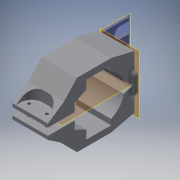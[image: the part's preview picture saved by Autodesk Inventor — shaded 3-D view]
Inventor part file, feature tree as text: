
AUTODESK INVENTOR PART (.ipt)
format: ipt  version: 2016 (Build 200138000, 138)  size: 446,464 bytes
history: native  units: in
note: dims shown in document units (in); Inventor stores cm internally (conversion verified against a paired STEP export)
features: sketch x12, extrude x11, projected_geometry x6, plane x4, reference x4, fillet x3, revolve x1
ambient origin geometry x8: Origin, YZ Plane, XZ Plane, XY Plane, X Axis, Y Axis, Z Axis, Center Point
bodies: Solid1 (feature_tree)
feature tree (41):
  plane  "Work Plane1"
  plane  "Work Plane2"
  extrude  "Extrusion1"  Depth=1.315in
  plane  "Work Plane3"
  extrude  "Extrusion2"  Depth=1.4in
  extrude  "Extrusion3"  Depth=1.8in TaperAngle=0.0deg
  plane  "Work Plane4"
  revolve  "Revolution1"  [1 undecoded]
  fillet  "Fillet1"  Radius=1.925in
  extrude  "Extrusion4"  TaperAngle=90.0deg  [1 undecoded]
  extrude  "Extrusion5"  Depth=0.2in TaperAngle=0.0deg
  extrude  "Extrusion6"  Depth=0.2in TaperAngle=0.0deg
  extrude  "Extrusion7"  Depth=2.575in TaperAngle=0.0deg
  extrude  "Extrusion8"  Depth=0.175in
  extrude  "Extrusion9"  Depth=0.2in TaperAngle=0.0deg
  fillet  "Fillet2"  Radius=0.2in
  fillet  "Fillet3"  Radius=0.625in
  extrude  "Extrusion10"  Depth=0.35in
  extrude  "Extrusion11"  Depth=0.2in
  sketch  "Sketch1"  dims[d2=0.6575in d3=1.315in]
  reference  "Reference1"
  sketch  "Sketch2"  dims[d10=2.92in d11=1.4in]
  sketch  "Sketch3"  dims[d12=0.35in d13=1.8in d14=0.0in]
  reference  "Reference2"
  sketch  "Sketch4"  dims[d15=0.5in d16=0.35in d17=1.925in d18=0.0in]
  reference  "Reference3"
  sketch  "Sketch5"  dims[d19=1.925in d20=0.0in d21=90.0deg]
  projected_geometry  "Projected Loop1"
  reference  "Reference4"
  sketch  "Sketch6"  dims[d22=0.3125in d23=0.2in d24=0.0in]
  projected_geometry  "Projected Loop2"
  sketch  "Sketch7"  dims[d25=1.5in d26=0.2in d27=0.0in]
  projected_geometry  "Projected Loop3"
  sketch  "Sketch8"  dims[d28=0.4in d29=2.575in d30=0.0in]
  projected_geometry  "Projected Loop4"
  sketch  "Sketch9"  dims[d31=0.175in d32=0.175in]
  sketch  "Sketch10"  dims[d33=2.575in d34=0.0in d35=0.2in d36=0.0in d37=0.2in d38=0.0in d39=0.625in]
  sketch  "Sketch11"  dims[d40=0.625in d41=0.35in]
  projected_geometry  "Projected Loop5"
  sketch  "Sketch12"  dims[d44=0.3in d45=0.2in d46=0.2in d47=0.4in d48=90.0deg d49=0.3in d50=10.0in d51=0.0in d52=0.2in d53=0.0in]
  projected_geometry  "Projected Loop6"
note: 2 required parameter values undecoded (feature->parameter linkage not recoverable at this tier; creation-order binding heuristic only, values carry confidence <= 0.55)